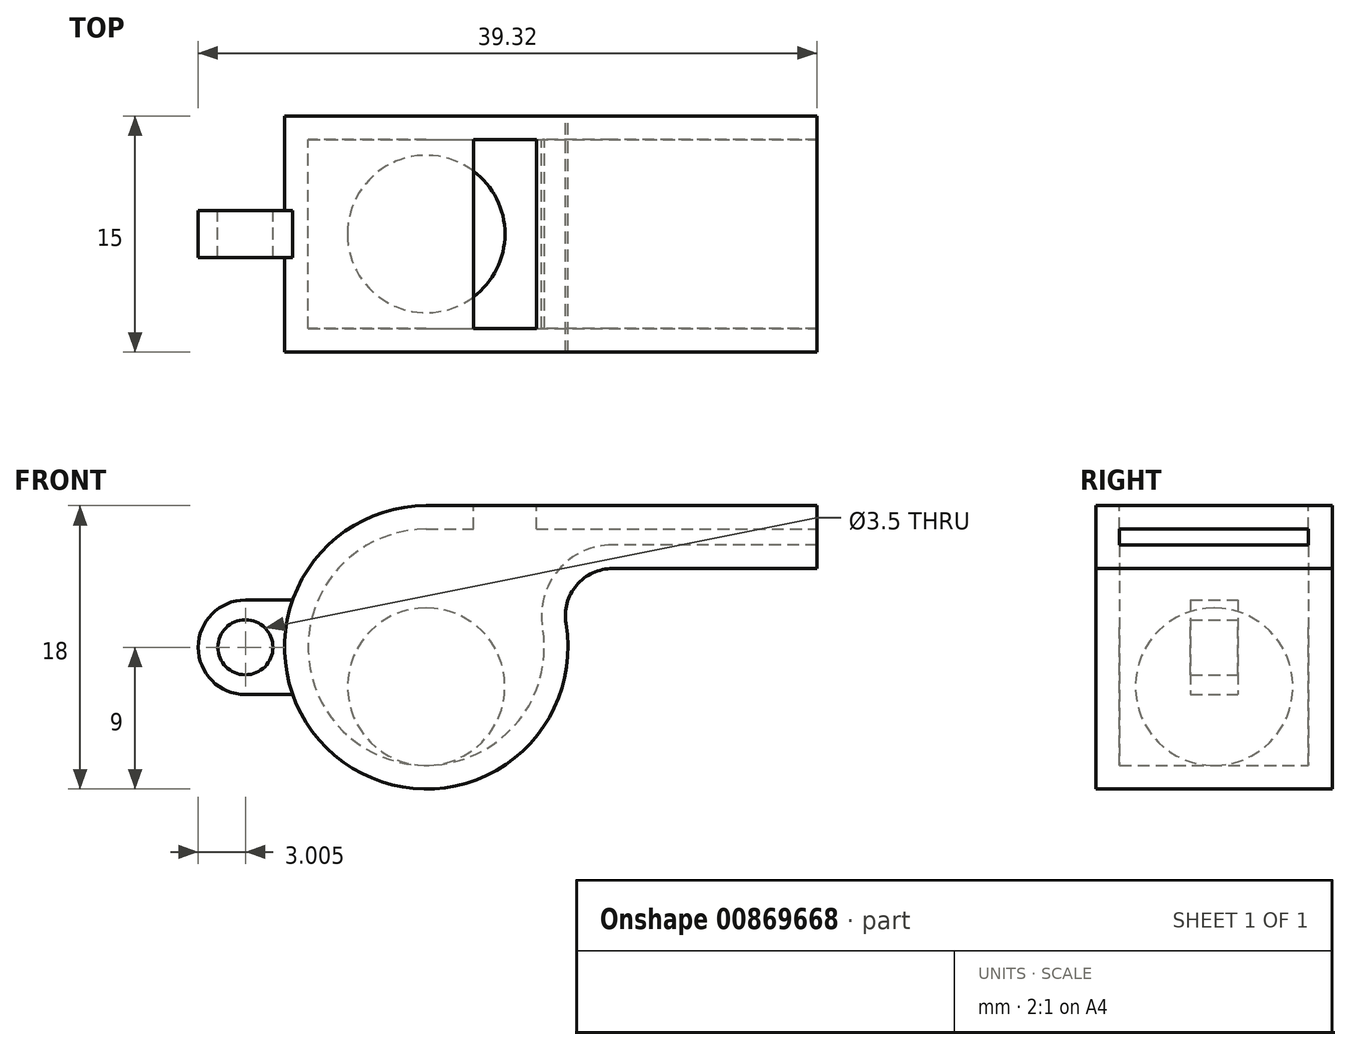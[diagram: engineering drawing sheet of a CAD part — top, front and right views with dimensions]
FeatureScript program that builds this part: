
annotation { "Feature Type Name" : "Feature", "Feature Type Description" : "" }
export const myFeature = defineFeature(function(context is Context, id is Id, definition is map)
    precondition{}
    {
        {
            var Q0;
            Q0=qCreatedBy(makeId("Front.planeOp"),FACE);
            var sketch = newSketch(context, id + "F0", { "sketchPlane" : qUnion([Q0])});
            skArc(sketch, "E0", {"start": v(0, 9) * mm, "mid": v(-5.8, -6.87) * mm, "end": v(8.87, 1.5) * mm});
            skLineSegment(sketch, "E1", {"start": v(0, 9) * mm, "end": v(24.83, 9) * mm});
            skLineSegment(sketch, "E2", {"start": v(24.83, 9) * mm, "end": v(24.83, 5) * mm});
            skLineSegment(sketch, "E3", {"start": v(24.83, 5) * mm, "end": v(11.83, 5) * mm});
            skPoint(sketch, "E4.visualSharp", {"position": v(7.48, 5) * mm});
            skArc(sketch, "E4.filletArc", {"start": v(11.83, 5) * mm, "mid": v(9.54, 3.94) * mm, "end": v(8.87, 1.5) * mm});
            skSolve(sketch);
        }
        {
            var Q0;
            Q0=makeQuery(id+"F0.imprint","IMPRINT",FACE,{"disambiguationData":[TD([[makeQuery(id+"F0.imprint","IMPRINT",EDGE,{"derivedFrom":sQuery(id+"F0.wireOp",EDGE,"E0")}),1.0]])]});
            extrude(context, id + "F1", {"entities" : qUnion([Q0]), "endBound" : BoundingType.SYMMETRIC, "depth" : 15 * mm, "offsetDistance" : 25 * mm});
        }
        {
            var Q0;
            Q0=makeQuery(id+"F1.opExtrude","SWEPT_FACE",FACE,{"disambiguationData":[OSD([sQuery(id+"F0.wireOp",EDGE,"E2")])]});
            shell(context, id + "F2", {"entities" : qUnion([Q0]), "thickness" : 1.5 * mm});
        }
        {
            var Q0;
            Q0=makeQuery(id+"F1.opExtrude","SWEPT_FACE",FACE,{"disambiguationData":[OSD([sQuery(id+"F0.wireOp",EDGE,"E1")])]});
            var sketch = newSketch(context, id + "F3", { "sketchPlane" : qUnion([Q0])});
            skLineSegment(sketch, "E5.bottom", {"start": v(3, 6) * mm, "end": v(7, 6) * mm});
            skLineSegment(sketch, "E5.top", {"start": v(3, -6) * mm, "end": v(7, -6) * mm});
            skLineSegment(sketch, "E5.left", {"start": v(3, 6) * mm, "end": v(3, -6) * mm});
            skLineSegment(sketch, "E5.right", {"start": v(7, 6) * mm, "end": v(7, -6) * mm});
            skSolve(sketch);
        }
        {
            var Q0;
            Q0=makeQuery(id+"F3.imprint","IMPRINT",FACE,{"disambiguationData":[TD([[makeQuery(id+"F3.imprint","IMPRINT",EDGE,{"derivedFrom":sQuery(id+"F3.wireOp",EDGE,"E5.bottom")}),-1.0]])]});
            extrude(context, id + "F4", {"entities" : qUnion([Q0]), "operationType" : NewBodyOperationType.REMOVE, "oppositeDirection" : true, "depth" : 1.5 * mm, "offsetDistance" : 25 * mm});
        }
        {
            var Q0;
            Q0=qCreatedBy(makeId("Front.planeOp"),FACE);
            var sketch = newSketch(context, id + "F5", { "sketchPlane" : qUnion([Q0])});
            skArc(sketch, "E6", {"start": v(-11.49, 3) * mm, "mid": v(-14.49, 0) * mm, "end": v(-11.49, -3) * mm});
            skLineSegment(sketch, "E7", {"start": v(-11.49, 3) * mm, "end": v(-8.49, 3) * mm});
            skLineSegment(sketch, "E8", {"start": v(-11.49, -3) * mm, "end": v(-8.49, -3) * mm});
            skCircle(sketch, "E9", {"center": v(-11.49, 0) * mm, "radius": 1.75 * mm});
            skLineSegment(sketch, "E10", {"start": v(-8.49, 3) * mm, "end": v(-8.49, -3) * mm});
            skSolve(sketch);
        }
        {
            var Q0;
            Q0 = qSketchRegion(id + "F5", true);
            extrude(context, id + "F6", {"entities" : qUnion([Q0]), "operationType" : NewBodyOperationType.ADD, "endBound" : BoundingType.SYMMETRIC, "depth" : 3 * mm, "offsetDistance" : 25 * mm});
        }
        {
            var Q0;
            Q0=qCreatedBy(makeId("Front.planeOp"),FACE);
            var sketch = newSketch(context, id + "F7", { "sketchPlane" : qUnion([Q0])});
            skArc(sketch, "E11", {"start": v(0, -7.5) * mm, "mid": v(5, -2.5) * mm, "end": v(0, 2.5) * mm});
            skLineSegment(sketch, "E12", {"start": v(0, 2.5) * mm, "end": v(0, -7.5) * mm});
            skSolve(sketch);
        }
        {
            var Q0;
            Q0 = qSketchRegion(id + "F7", true);
            var Q1;
            Q1 = qConstructionFilter(qBodyType(qCreatedBy(id + "F7" ,EDGE), BodyType.WIRE), ConstructionObject.NO);
            var Q2;
            Q2=sQuery(id+"F7.wireOp",EDGE,"E12");
            revolve(context, id + "F8", {"surfaceOperationType" : NewSurfaceOperationType.NEW, "entities" : qUnion([Q0]), "surfaceEntities" : qUnion([Q1]), "axis" : qUnion([Q2]), "revolveType" : RevolveType.FULL});
        }
    });
